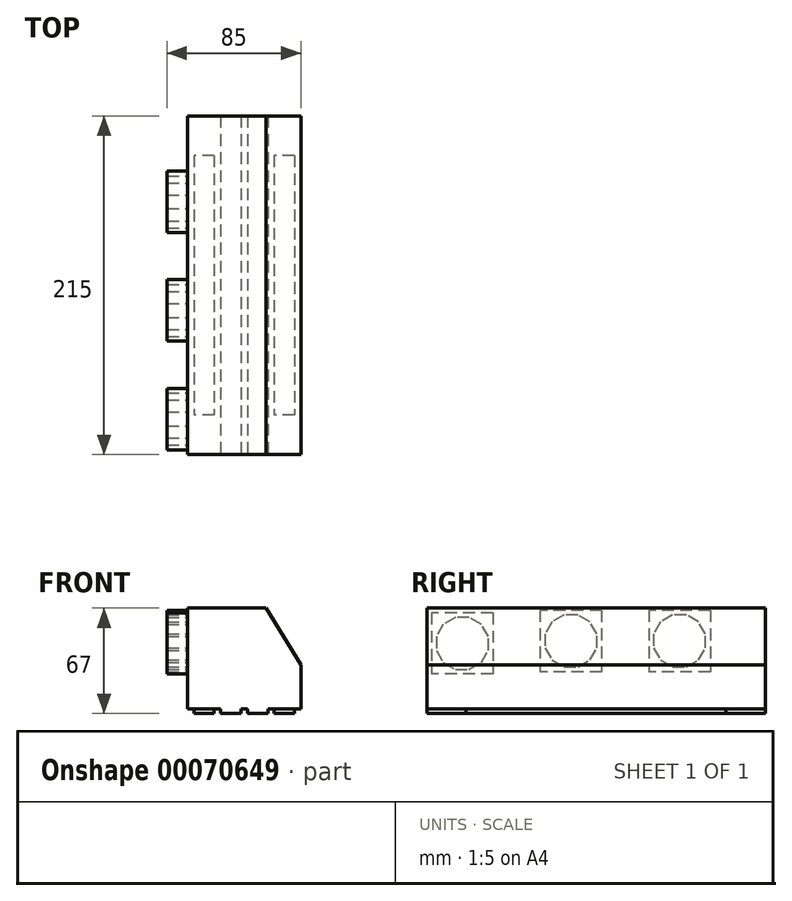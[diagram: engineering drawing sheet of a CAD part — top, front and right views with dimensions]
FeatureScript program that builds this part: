
annotation { "Feature Type Name" : "Feature", "Feature Type Description" : "" }
export const myFeature = defineFeature(function(context is Context, id is Id, definition is map)
    precondition{}
    {
        {
            var Q0;
            Q0=qCreatedBy(makeId("Front.planeOp"),FACE);
            var sketch = newSketch(context, id + "F0", { "sketchPlane" : qUnion([Q0])});
            skLineSegment(sketch, "E0.bottom", {"start": v(0, 0) * mm, "end": v(72, 0) * mm});
            skLineSegment(sketch, "E0.top", {"start": v(0, 64) * mm, "end": v(50, 64) * mm});
            skLineSegment(sketch, "E0.left", {"start": v(0, 0) * mm, "end": v(0, 64) * mm});
            skLineSegment(sketch, "E0.right", {"start": v(72, 0) * mm, "end": v(72, 28) * mm});
            skLineSegment(sketch, "E1", {"start": v(50, 64) * mm, "end": v(72, 28) * mm});
            skSolve(sketch);
        }
        {
            var Q0;
            Q0 = qSketchRegion(id + "F0", true);
            extrude(context, id + "F1", {"entities" : qUnion([Q0]), "oppositeDirection" : true, "depth" : 215 * mm});
        }
        {
            var Q0;
            Q0=makeQuery(id+"F1.opExtrude","SWEPT_FACE",FACE,{"disambiguationData":[OSD([sQuery(id+"F0.wireOp",EDGE,"E0.left")])]});
            var sketch = newSketch(context, id + "F2", { "sketchPlane" : qUnion([Q0])});
            skLineSegment(sketch, "E2.bottom", {"start": v(-42, 61) * mm, "end": v(-3, 61) * mm});
            skLineSegment(sketch, "E2.top", {"start": v(-42, 22) * mm, "end": v(-3, 22) * mm});
            skLineSegment(sketch, "E2.left", {"start": v(-42, 61) * mm, "end": v(-42, 22) * mm});
            skLineSegment(sketch, "E2.right", {"start": v(-3, 61) * mm, "end": v(-3, 22) * mm});
            skPoint(sketch, "E3", {"position": v(-22.5, 41.5) * mm});
            skPoint(sketch, "E3.positionSnap0", {"position": v(-22.5, 61) * mm});
            skPoint(sketch, "E3.positionSnap1", {"position": v(-42, 41.5) * mm});
            skLineSegment(sketch, "E4.0", {"start": v(-18.08, 58) * mm, "end": v(-10.42, 53.58) * mm});
            skLineSegment(sketch, "E4.1", {"start": v(-10.42, 53.58) * mm, "end": v(-6, 45.92) * mm});
            skLineSegment(sketch, "E4.2", {"start": v(-6, 45.92) * mm, "end": v(-6, 37.08) * mm});
            skLineSegment(sketch, "E4.3", {"start": v(-6, 37.08) * mm, "end": v(-10.42, 29.42) * mm});
            skLineSegment(sketch, "E4.4", {"start": v(-10.42, 29.42) * mm, "end": v(-18.08, 25) * mm});
            skLineSegment(sketch, "E4.5", {"start": v(-18.08, 25) * mm, "end": v(-26.92, 25) * mm});
            skLineSegment(sketch, "E4.6", {"start": v(-26.92, 25) * mm, "end": v(-34.58, 29.42) * mm});
            skLineSegment(sketch, "E4.7", {"start": v(-34.58, 29.42) * mm, "end": v(-39, 37.08) * mm});
            skLineSegment(sketch, "E4.8", {"start": v(-39, 37.08) * mm, "end": v(-39, 45.92) * mm});
            skLineSegment(sketch, "E4.9", {"start": v(-39, 45.92) * mm, "end": v(-34.58, 53.58) * mm});
            skLineSegment(sketch, "E4.10", {"start": v(-34.58, 53.58) * mm, "end": v(-26.92, 58) * mm});
            skLineSegment(sketch, "E4.11", {"start": v(-26.92, 58) * mm, "end": v(-18.08, 58) * mm});
            skPoint(sketch, "E4.0.midPoint", {"position": v(-14.25, 55.79) * mm});
            skSolve(sketch);
        }
        {
            var Q0;
            Q0 = qSketchRegion(id + "F2", true);
            extrude(context, id + "F3", {"entities" : qUnion([Q0]), "operationType" : NewBodyOperationType.ADD, "depth" : 13 * mm});
        }
        {
            var Q0;
            {var subQ3=sQuery(id+"F0.wireOp",EDGE,"E0.left");var subQ4=sQuery(id+"F0.wireOp",EDGE,"E0.bottom");Q0=makeQuery(id+"F3.boolean.opBoolean","SPLIT",FACE,{"disambiguationData":[TD([makeQuery(id+"F1.opExtrude","SWEPT_FACE",FACE,{"disambiguationData":[OSD([subQ4])]})])],"derivedFrom":makeQuery(id+"F1.opExtrude","SWEPT_FACE",FACE,{"disambiguationData":[OSD([subQ3])]})});}
            var sketch = newSketch(context, id + "F4", { "sketchPlane" : qUnion([Q0])});
            skLineSegment(sketch, "E5.bottom", {"start": v(-111, 62.56) * mm, "end": v(-72, 62.56) * mm});
            skLineSegment(sketch, "E5.top", {"start": v(-111, 23.56) * mm, "end": v(-72, 23.56) * mm});
            skLineSegment(sketch, "E5.left", {"start": v(-111, 62.56) * mm, "end": v(-111, 23.56) * mm});
            skLineSegment(sketch, "E5.right", {"start": v(-72, 62.56) * mm, "end": v(-72, 23.56) * mm});
            skPoint(sketch, "E6", {"position": v(-91.5, 43.06) * mm});
            skPoint(sketch, "E6.positionSnap0", {"position": v(-91.5, 62.56) * mm});
            skPoint(sketch, "E6.positionSnap1", {"position": v(-111, 43.06) * mm});
            skLineSegment(sketch, "E7.0", {"start": v(-87.08, 59.56) * mm, "end": v(-79.42, 55.13) * mm});
            skLineSegment(sketch, "E7.1", {"start": v(-79.42, 55.13) * mm, "end": v(-75, 47.48) * mm});
            skLineSegment(sketch, "E7.2", {"start": v(-75, 47.48) * mm, "end": v(-75, 38.63) * mm});
            skLineSegment(sketch, "E7.3", {"start": v(-75, 38.63) * mm, "end": v(-79.42, 30.98) * mm});
            skLineSegment(sketch, "E7.4", {"start": v(-79.42, 30.98) * mm, "end": v(-87.08, 26.56) * mm});
            skLineSegment(sketch, "E7.5", {"start": v(-87.08, 26.56) * mm, "end": v(-95.92, 26.56) * mm});
            skLineSegment(sketch, "E7.6", {"start": v(-95.92, 26.56) * mm, "end": v(-103.58, 30.98) * mm});
            skLineSegment(sketch, "E7.7", {"start": v(-103.58, 30.98) * mm, "end": v(-108, 38.63) * mm});
            skLineSegment(sketch, "E7.8", {"start": v(-108, 38.63) * mm, "end": v(-108, 47.48) * mm});
            skLineSegment(sketch, "E7.9", {"start": v(-108, 47.48) * mm, "end": v(-103.58, 55.13) * mm});
            skLineSegment(sketch, "E7.10", {"start": v(-103.58, 55.13) * mm, "end": v(-95.92, 59.56) * mm});
            skLineSegment(sketch, "E7.11", {"start": v(-95.92, 59.56) * mm, "end": v(-87.08, 59.56) * mm});
            skPoint(sketch, "E7.0.midPoint", {"position": v(-83.25, 57.34) * mm});
            skLineSegment(sketch, "E8.bottom", {"start": v(-180, 62.55) * mm, "end": v(-141, 62.55) * mm});
            skLineSegment(sketch, "E8.top", {"start": v(-180, 23.55) * mm, "end": v(-141, 23.55) * mm});
            skLineSegment(sketch, "E8.left", {"start": v(-180, 62.55) * mm, "end": v(-180, 23.55) * mm});
            skLineSegment(sketch, "E8.right", {"start": v(-141, 62.55) * mm, "end": v(-141, 23.55) * mm});
            skPoint(sketch, "E9", {"position": v(-160.5, 43.05) * mm});
            skPoint(sketch, "E9.positionSnap0", {"position": v(-160.5, 62.55) * mm});
            skPoint(sketch, "E9.positionSnap1", {"position": v(-180, 43.05) * mm});
            skLineSegment(sketch, "E10.0", {"start": v(-156.08, 59.55) * mm, "end": v(-148.42, 55.12) * mm});
            skLineSegment(sketch, "E10.1", {"start": v(-148.42, 55.12) * mm, "end": v(-144, 47.47) * mm});
            skLineSegment(sketch, "E10.2", {"start": v(-144, 47.47) * mm, "end": v(-144, 38.62) * mm});
            skLineSegment(sketch, "E10.3", {"start": v(-144, 38.62) * mm, "end": v(-148.42, 30.97) * mm});
            skLineSegment(sketch, "E10.4", {"start": v(-148.42, 30.97) * mm, "end": v(-156.08, 26.55) * mm});
            skLineSegment(sketch, "E10.5", {"start": v(-156.08, 26.55) * mm, "end": v(-164.92, 26.55) * mm});
            skLineSegment(sketch, "E10.6", {"start": v(-164.92, 26.55) * mm, "end": v(-172.58, 30.97) * mm});
            skLineSegment(sketch, "E10.7", {"start": v(-172.58, 30.97) * mm, "end": v(-177, 38.62) * mm});
            skLineSegment(sketch, "E10.8", {"start": v(-177, 38.62) * mm, "end": v(-177, 47.47) * mm});
            skLineSegment(sketch, "E10.9", {"start": v(-177, 47.47) * mm, "end": v(-172.58, 55.12) * mm});
            skLineSegment(sketch, "E10.10", {"start": v(-172.58, 55.12) * mm, "end": v(-164.92, 59.55) * mm});
            skLineSegment(sketch, "E10.11", {"start": v(-164.92, 59.55) * mm, "end": v(-156.08, 59.55) * mm});
            skPoint(sketch, "E10.0.midPoint", {"position": v(-152.25, 57.33) * mm});
            skSolve(sketch);
        }
        {
            var Q0;
            Q0 = qSketchRegion(id + "F4", true);
            var Q1;
            Q1=makeQuery(id+"F3.opExtrude","CAP_FACE",FACE,{"disambiguationData":[OSD([sQuery(id+"F2.wireOp",EDGE,"E2.bottom"),sQuery(id+"F2.wireOp",EDGE,"E2.top"),sQuery(id+"F2.wireOp",EDGE,"E2.left"),sQuery(id+"F2.wireOp",EDGE,"E2.right"),sQuery(id+"F2.wireOp",EDGE,"E4.0"),sQuery(id+"F2.wireOp",EDGE,"E4.1"),sQuery(id+"F2.wireOp",EDGE,"E4.2"),sQuery(id+"F2.wireOp",EDGE,"E4.3"),sQuery(id+"F2.wireOp",EDGE,"E4.4"),sQuery(id+"F2.wireOp",EDGE,"E4.5"),sQuery(id+"F2.wireOp",EDGE,"E4.6"),sQuery(id+"F2.wireOp",EDGE,"E4.7"),sQuery(id+"F2.wireOp",EDGE,"E4.8"),sQuery(id+"F2.wireOp",EDGE,"E4.9"),sQuery(id+"F2.wireOp",EDGE,"E4.10"),sQuery(id+"F2.wireOp",EDGE,"E4.11")])],"isStart":false});
            extrude(context, id + "F5", {"entities" : qUnion([Q0]), "operationType" : NewBodyOperationType.ADD, "endBound" : BoundingType.UP_TO_SURFACE, "endBoundEntityFace" : qUnion([Q1]), "depth" : 25 * mm});
        }
        {
            var Q0;
            Q0=makeQuery(id+"F1.opExtrude","SWEPT_FACE",FACE,{"disambiguationData":[OSD([sQuery(id+"F0.wireOp",EDGE,"E0.bottom")])]});
            var sketch = newSketch(context, id + "F6", { "sketchPlane" : qUnion([Q0])});
            skLineSegment(sketch, "E11.bottom", {"start": v(51, -215) * mm, "end": v(38, -215) * mm});
            skLineSegment(sketch, "E11.top", {"start": v(51, 0) * mm, "end": v(38, 0) * mm});
            skLineSegment(sketch, "E11.left", {"start": v(51, -215) * mm, "end": v(51, 0) * mm});
            skLineSegment(sketch, "E11.right", {"start": v(38, -215) * mm, "end": v(38, 0) * mm});
            skLineSegment(sketch, "E12.1.0.0", {"start": v(34, -215) * mm, "end": v(34, 0) * mm});
            skLineSegment(sketch, "E12.1.0.1", {"start": v(34, -215) * mm, "end": v(21, -215) * mm});
            skLineSegment(sketch, "E12.1.0.2", {"start": v(21, -215) * mm, "end": v(21, 0) * mm});
            skLineSegment(sketch, "E12.1.0.3", {"start": v(34, 0) * mm, "end": v(21, 0) * mm});
            skLineSegment(sketch, "E12.direction1", {"start": v(38, -215) * mm, "end": v(21, -215) * mm});
            skLineSegment(sketch, "E13.bottom", {"start": v(17, -190) * mm, "end": v(4, -190) * mm});
            skLineSegment(sketch, "E13.top", {"start": v(17, -25) * mm, "end": v(4, -25) * mm});
            skLineSegment(sketch, "E13.left", {"start": v(17, -190) * mm, "end": v(17, -25) * mm});
            skLineSegment(sketch, "E13.right", {"start": v(4, -190) * mm, "end": v(4, -25) * mm});
            skLineSegment(sketch, "E14.left", {"start": v(68, -190) * mm, "end": v(68, -25) * mm});
            skLineSegment(sketch, "E14.top", {"start": v(68, -25) * mm, "end": v(55, -25) * mm});
            skLineSegment(sketch, "E14.right", {"start": v(55, -190) * mm, "end": v(55, -25) * mm});
            skLineSegment(sketch, "E14.bottom", {"start": v(68, -190) * mm, "end": v(55, -190) * mm});
            skLineSegment(sketch, "E15", {"start": v(72, -107.5) * mm, "end": v(0, -107.5) * mm, "construction": true});
            skPoint(sketch, "E16", {"position": v(68, -107.5) * mm});
            skLineSegment(sketch, "E17", {"start": v(36, 0) * mm, "end": v(36, -215) * mm, "construction": true});
            skLineSegment(sketch, "E18.0", {"start": v(0, -185) * mm, "end": v(4, -185) * mm, "construction": true});
            skLineSegment(sketch, "E19", {"start": v(17, -185) * mm, "end": v(21, -185) * mm, "construction": true});
            skLineSegment(sketch, "E20.trimOffspring", {"start": v(34, -185) * mm, "end": v(38, -185) * mm, "construction": true});
            skLineSegment(sketch, "E21.trimOffspring", {"start": v(51, -185) * mm, "end": v(55, -185) * mm, "construction": true});
            skLineSegment(sketch, "E22.trimOffspring", {"start": v(68, -185) * mm, "end": v(72, -185) * mm, "construction": true});
            skSolve(sketch);
        }
        {
            var Q0;
            Q0 = qSketchRegion(id + "F6", true);
            extrude(context, id + "F7", {"entities" : qUnion([Q0]), "operationType" : NewBodyOperationType.ADD, "flatOperationType" : FlatOperationType.REMOVE, "offsetDistance" : 25 * mm, "depth" : 3 * mm, "domain" : OperationDomain.MODEL});
        }
    });
